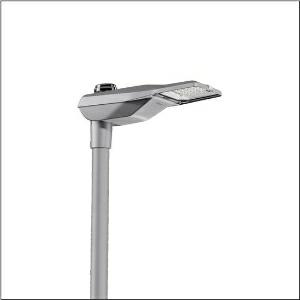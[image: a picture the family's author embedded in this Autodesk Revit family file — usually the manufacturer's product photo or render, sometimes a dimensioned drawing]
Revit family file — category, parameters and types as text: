
# Revit family: streetlight_sl_21_micro___st0_8a_5xe5c37n08db_0c9a
name_source: partatom
category: Lighting Fixtures
units: mm (PartAtom-declared; Revit-internal decimal feet)

## family parameters
Cut with Voids When Loaded = No
Host = Face
Light Source = No
Part Type = Normal
Room Calculation Point = No
Round Connector Dimension = Use Diameter
Shared = No

## types (1)
- --- (1 x LED, 5110 lm, 39.1 W, 3000K)
    Apparent Load = 39 VA
    CIE Flux Codes = 38 75 97 100 100
    Color Rendering = 70
    Color Temperature = 3000K
    Default Elevation = 1800 mm
    Description = Streetlight SL 21 micro, mast luminaire, primary light control with lens, of PMMA, primary optical cover: cover, of toughened safety glass, transparent, light distribution: ST0.8a, light emission: direct distribution, primary light characteristic: asymmetric, installation type: post-top, LED, 3G 1.5mm², High Power LED, rated luminous flux: 5.110lm, luminous efficacy: 131lm/W, light colour: 730, colour temperature: 3000K, control gear: NEMA (7pin), control: overheat protection, pre-setting: linear dimming characteristic, constant luminous flux control, time-dependent luminous flux control, flexible luminous flux parameterisation, mains connection: 230..240V, AC, 50/60Hz, connection cable pre-assembled, cable length: 6,5m, wiring characteristics: H07RN-F, start of lifetime: 39W, end of service life: 41W, reduction: 18W, luminaire housing, of diecast aluminium (EN AC-44300), powder-coated, Siteco® metallic grey (DB 702S), corrosivity category C5 mid according to DIN EN ISO 12944, multi-level sealing system, sealing non-destructively replaceable, inclination adjustable: 0°, 5°, 10°, 15°, length: 528mm, width: 235mm, height: 110mm, spigot size: 76/60mm (post-top), mounting height: 4..8m, protection rating (complete): IP66, insulation class (complete): insulation class I (protective earthing), certification: CE, ENEC, ENEC+, VDE, impact resistance: IK10, permissible operating ambient temperature for outdoor applications: -40..+50°C, standard-compliant lighting for roads and squares, packaging unit: 1 piece

Light Distribution: ST0.8a
    Height = 110 mm
    Lamp = 1 x LED
    Lamp Light Flux = 5110 lm
    Lamp Power = 39.1 W
    Lamp count = 1
    Length = 528 mm
    Luminous efficacy = 131 lm/W
    Manufacturer = Siteco
    ModVariant = No
    Model = 5XE5C37N08DB
    Number of Poles = 1
    OnlyDefault = Yes
    Power Factor = 1
    Product Name = Streetlight SL 21 micro | ST0.8a
    Product group = mast luminaire | pylon top
    ProductGroupID = 6100
    Protection Class = Protection class I
    Protection Degree = IP 66
    RLX_Detail_Level = 1
    RLX_Emergency_Light_Flux = 0 lm
    RLX_Emergency_Type = 0
    RLX_Emergency_Type_DB = No
    RlxData = <blob elided: 98829 chars, md5=82f5ff89>
    Socket = socket
    Standby Power = 0 W
    System Light Flux = 5110 lm
    System Power = 39 W
    Type Comments = factory setting: luminous flux: 100 % | dim-lin: 254 | 765 mA
    Type Image = l_1294375.jpg
    URL = http://relux.com
    VarID = @adj_155853
    Voltage = 0 V
    Weight = 0.00 kg
    Width = 235 mm

## geometry (parser evidence)
native form markers: Blend x4, Sweep x9
no freeform markers — native parametric forms only
